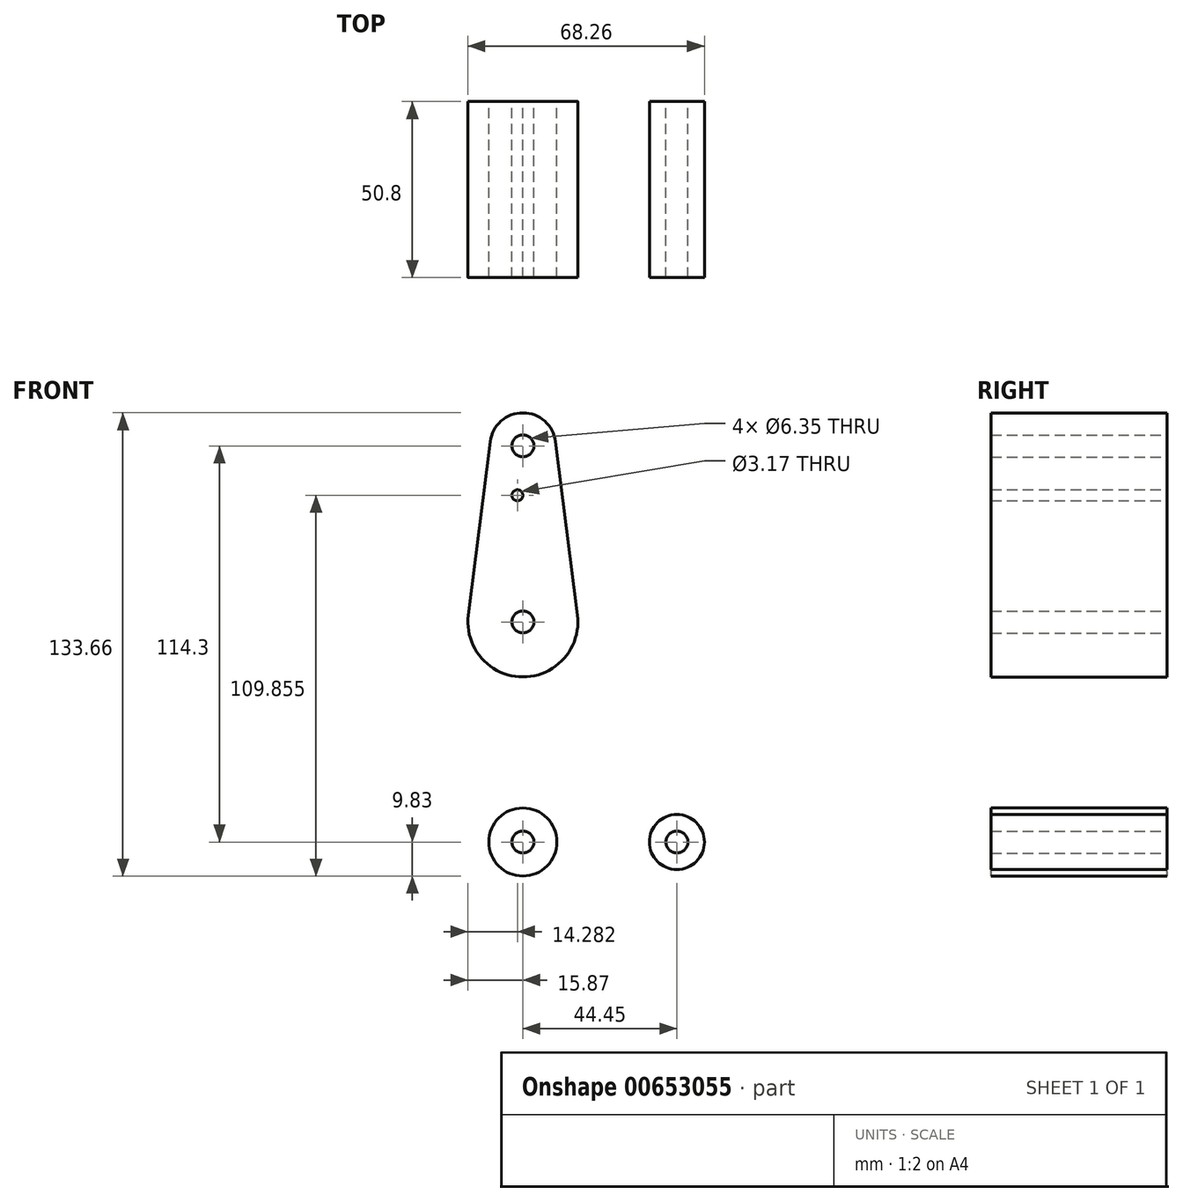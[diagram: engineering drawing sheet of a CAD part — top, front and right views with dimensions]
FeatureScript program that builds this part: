
annotation { "Feature Type Name" : "Feature", "Feature Type Description" : "" }
export const myFeature = defineFeature(function(context is Context, id is Id, definition is map)
    precondition{}
    {
        {
            var Q0;
            Q0=qCreatedBy(makeId("Front.planeOp"),FACE);
            var sketch = newSketch(context, id + "F0", { "sketchPlane" : qUnion([Q0])});
            skCircle(sketch, "E0", {"center": v(0, 0) * mm, "radius": 9.83 * mm});
            skLineSegment(sketch, "E1", {"start": v(0, 0) * mm, "end": v(0, 63.5) * mm});
            skCircle(sketch, "E2", {"center": v(0, 63.5) * mm, "radius": 15.88 * mm});
            skLineSegment(sketch, "E3", {"start": v(0, 63.5) * mm, "end": v(0, 114.3) * mm});
            skCircle(sketch, "E4", {"center": v(0, 114.3) * mm, "radius": 9.53 * mm});
            skLineSegment(sketch, "E5", {"start": v(0, 0) * mm, "end": v(44.45, 0) * mm});
            skCircle(sketch, "E6", {"center": v(44.45, 0) * mm, "radius": 7.94 * mm});
            skLineSegment(sketch, "E7", {"start": v(0, -9.83) * mm, "end": v(44.79, -7.93) * mm});
            skPoint(sketch, "E8.newPointA", {"position": v(9.9, 0.3) * mm});
            skCircle(sketch, "E9", {"center": v(0, 114.3) * mm, "radius": 3.18 * mm});
            skCircle(sketch, "E10", {"center": v(0, 63.5) * mm, "radius": 3.18 * mm});
            skCircle(sketch, "E11", {"center": v(0, 0) * mm, "radius": 3.18 * mm});
            skCircle(sketch, "E12", {"center": v(44.45, 0) * mm, "radius": 3.18 * mm});
            skCircle(sketch, "E13", {"center": v(-1.59, 100.03) * mm, "radius": 1.59 * mm});
            skLineSegment(sketch, "E14", {"start": v(-9.45, 115.5) * mm, "end": v(-15.75, 65.48) * mm});
            skLineSegment(sketch, "E15", {"start": v(-15.8, 61.99) * mm, "end": v(-9.87, 0) * mm});
            skLineSegment(sketch, "E16", {"start": v(9.45, 115.5) * mm, "end": v(15.75, 65.48) * mm});
            skLineSegment(sketch, "E17", {"start": v(15.8, 61.99) * mm, "end": v(11.57, 17.72) * mm});
            skPoint(sketch, "E18.end.orphan", {"position": v(44.79, 7.93) * mm});
            skLineSegment(sketch, "E19", {"start": v(19.14, 9.02) * mm, "end": v(44.79, 7.93) * mm});
            skArc(sketch, "E20.filletArc", {"start": v(11.57, 17.72) * mm, "mid": v(13.49, 11.74) * mm, "end": v(19.14, 9.02) * mm});
            skSolve(sketch);
        }
        {
            var Q0;
            {var subQ0=sQuery(id+"F0.wireOp",EDGE,"E7");var subQ1=sQuery(id+"F0.wireOp",EDGE,"E0");var subQ2=makeQuery(id+"F0.imprint","INTERSECT",VERTEX,{"disambiguationData":[OD(0.0)],"derivedFrom":[subQ1,subQ0]});Q0=makeQuery(id+"F0.imprint","IMPRINT",FACE,{"disambiguationData":[TD([[makeQuery(id+"F0.imprint","IMPRINT",EDGE,{"disambiguationData":[TD([[subQ2,-1.0]])],"derivedFrom":subQ1}),1.0]])]});}
            var Q1;
            {var subQ0=sQuery(id+"F0.wireOp",EDGE,"E1");var subQ1=sQuery(id+"F0.wireOp",EDGE,"E0");var subQ2=makeQuery(id+"F0.imprint","INTERSECT",VERTEX,{"derivedFrom":[subQ1,subQ0]});Q1=makeQuery(id+"F0.imprint","IMPRINT",FACE,{"disambiguationData":[TD([[makeQuery(id+"F0.imprint","IMPRINT",EDGE,{"disambiguationData":[TD([[subQ2,1.0]])],"derivedFrom":subQ1}),1.0]])]});}
            var Q2;
            {var subQ0=sQuery(id+"F0.wireOp",EDGE,"E7");var subQ1=sQuery(id+"F0.wireOp",EDGE,"E0");var subQ2=makeQuery(id+"F0.imprint","INTERSECT",VERTEX,{"disambiguationData":[OD(1.0)],"derivedFrom":[subQ1,subQ0]});Q2=makeQuery(id+"F0.imprint","IMPRINT",FACE,{"disambiguationData":[TD([[makeQuery(id+"F0.imprint","IMPRINT",EDGE,{"disambiguationData":[TD([[subQ2,-1.0]])],"derivedFrom":subQ1}),-1.0]])]});}
            var Q3;
            {var subQ0=sQuery(id+"F0.wireOp",EDGE,"E2");var subQ2=makeQuery(id+"F0.imprint","IMPRINT",VERTEX,{"derivedFrom":subQ0});Q3=makeQuery(id+"F0.imprint","IMPRINT",FACE,{"disambiguationData":[TD([[makeQuery(id+"F0.imprint","IMPRINT",EDGE,{"disambiguationData":[TD([[subQ2,1.0]])],"derivedFrom":subQ0}),1.0]])]});}
            var Q4;
            {var subQ0=sQuery(id+"F0.wireOp",EDGE,"E16");Q4=makeQuery(id+"F0.imprint","IMPRINT",FACE,{"disambiguationData":[TD([[makeQuery(id+"F0.imprint","IMPRINT",EDGE,{"derivedFrom":subQ0}),-1.0]])]});}
            var Q5;
            Q5=makeQuery(id+"F0.imprint","IMPRINT",FACE,{"disambiguationData":[TD([[makeQuery(id+"F0.imprint","IMPRINT",EDGE,{"derivedFrom":sQuery(id+"F0.wireOp",EDGE,"E9")}),-1.0]])]});
            var Q6;
            Q6=makeQuery(id+"F0.imprint","IMPRINT",FACE,{"disambiguationData":[TD([[makeQuery(id+"F0.imprint","IMPRINT",EDGE,{"derivedFrom":sQuery(id+"F0.wireOp",EDGE,"E12")}),-1.0]])]});
            var Q7;
            {var subQ1=sQuery(id+"F0.wireOp",EDGE,"E0");var subQ8=sQuery(id+"F0.wireOp",EDGE,"E7");var subQ9=makeQuery(id+"F0.imprint","INTERSECT",VERTEX,{"disambiguationData":[OD(0.0)],"derivedFrom":[subQ1,subQ8]});Q7=makeQuery(id+"F0.imprint","IMPRINT",FACE,{"disambiguationData":[TD([[makeQuery(id+"F0.imprint","IMPRINT",EDGE,{"disambiguationData":[TD([[subQ9,1.0]])],"derivedFrom":subQ1}),1.0]])]});}
            var Q8;
            {var subQ0=sQuery(id+"F0.wireOp",EDGE,"E2");var subQ2=sQuery(id+"F0.wireOp",EDGE,"E1");var subQ3=makeQuery(id+"F0.imprint","INTERSECT",VERTEX,{"derivedFrom":[subQ2,subQ0]});Q8=makeQuery(id+"F0.imprint","IMPRINT",FACE,{"disambiguationData":[TD([[makeQuery(id+"F0.imprint","IMPRINT",EDGE,{"disambiguationData":[TD([[subQ3,-1.0]])],"derivedFrom":subQ2}),-1.0]])]});}
            var Q9;
            {var subQ0=sQuery(id+"F0.wireOp",EDGE,"E13");Q9=makeQuery(id+"F0.imprint","IMPRINT",FACE,{"disambiguationData":[TD([[makeQuery(id+"F0.imprint","IMPRINT",EDGE,{"derivedFrom":subQ0}),-1.0]])]});}
            extrude(context, id + "F1", {"entities" : qUnion([Q0, Q1, Q2, Q3, Q4, Q5, Q6, Q7, Q8, Q9]), "depth" : 50.8 * mm, "offsetDistance" : 25.4 * mm});
        }
    });
